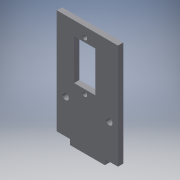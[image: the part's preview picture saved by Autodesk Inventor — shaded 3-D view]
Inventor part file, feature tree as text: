
AUTODESK INVENTOR PART (.ipt)
format: ipt  version: 2018 (Build 220112000, 112)  size: 126,976 bytes
history: native  units: in
note: dims shown in document units (in); Inventor stores cm internally (conversion verified against a paired STEP export)
features: reference x13, other x7, extrude x2, sketch x2
ambient origin geometry x8: Origin, YZ Plane, XZ Plane, XY Plane, X Axis, Y Axis, Z Axis, Center Point
bodies: Solid1 (feature_tree)
feature tree (24):
  extrude  "Extrusion1"  Depth=0.1181in
  extrude  "Extrusion2"  Depth=0.3937in
  sketch  "Sketch1"  dims[d0=2.3622in d1=0.1181in]
  reference  "Reference1"
  reference  "Reference2"
  reference  "Reference3"
  reference  "Reference4"
  reference  "Reference5"
  reference  "Reference6"
  reference  "Reference7"
  reference  "Reference8"
  reference  "Reference9"
  reference  "Reference10"
  reference  "Reference11"
  sketch  "Sketch2"  dims[d2=0.3937in d3=0.3937in d4=0.0039in d5=0.0039in d6=0.0039in d7=0.0039in d8=0.1181in d9=0.0in d10=0.2431in d11=0.0in]
  reference  "Reference12"
  reference  "Reference13"
  other  "Camera pan and tilt assembly.iam"
  other  "Servo motor:2"
  other  "Servo body:1"
  other  "Camera mount side bars:2"
  other  "Camera mount side bars:1"
  other  "Angle bracket long:1"
  other  "Angle bracket long:2"
